# Revit family: QF_ELECTROLUXPROFESSIONAL_1LSNLG_IC64832R_E
name_source: partatom
category: Attrezzature speciali
units: mm (PartAtom-declared; Revit-internal decimal feet)

## family parameters
Basato su piano di lavoro = No
Condiviso = No
Punto di calcolo locali = No
Quota connettore circolare = Usa diametro
Sempre verticale = Sì
Taglio con vuoti quando caricato = No
Tipo di parte = Normale

## types (5) — shared parameters
Cycle = 50 Hz
Depth Actual = 1620 mm
Height Actual = 1270 mm  [stored 4.16667 ft]
Latent Heat Output = 0.0
Length Actual = 3835 mm
Modello = IC64832R
Phase = 3
Produttore = Electrolux Professional
Sensible Heat Output = 0.0
URL = www.electroluxprofessional.com
Volts = 400 V
Watts = 54800 W
Weight = 1180
zero-valued in all types: Gas KW, Prospetto di default, Steam Pounds per Hour

## per-type parameters (varying)
| type | Descrizione | Item Number |
| 9882030145 | IRONER CYLINDER IC64832R REAR DELIVERY 3170MM PERFORMANCE EL. CE 400/50/3 DUBIXIUM ML VAC.FEED.TABLE | 1L0GRA |
| 9882030201 | IRONER CYLINDER IC64832R REAR DELIVERY 3170MM ACTIVE EL. CE 400/50/3 6MM SST CYL. FR FEED NOW | 1L8270 |
| 9882030237 | IRONER CYLINDER IC64832R REAR DELIVERY 3170MM EL. CE 400/50/3 DUBIXIUM ML VAC.FEED.TABLE DIAMMS | 1L0GW2 |
| 9882030128 | IRONER CYLINDER IC64832R REAR DELIVERY 3170MM PERFORMANCE EL. CE 400/50/3 DUBIXIUM FR VAC.FEED.TABLE | 1L0GMV |
| 9882030129 | IRONER CYLINDER IC64832R REAR DELIVERY 3170MM SUPERIOR EL. CE 400/50/3 DUBIXIUM FR FEED ALONE VAC.FEED.TABLE | 1L0GMW |

note: [stored X ft] marks values corroborated as IEEE doubles in the binary element streams (Revit-internal decimal feet)

## geometry (parser evidence)
native form markers: Sweep x11
no freeform markers — native parametric forms only
